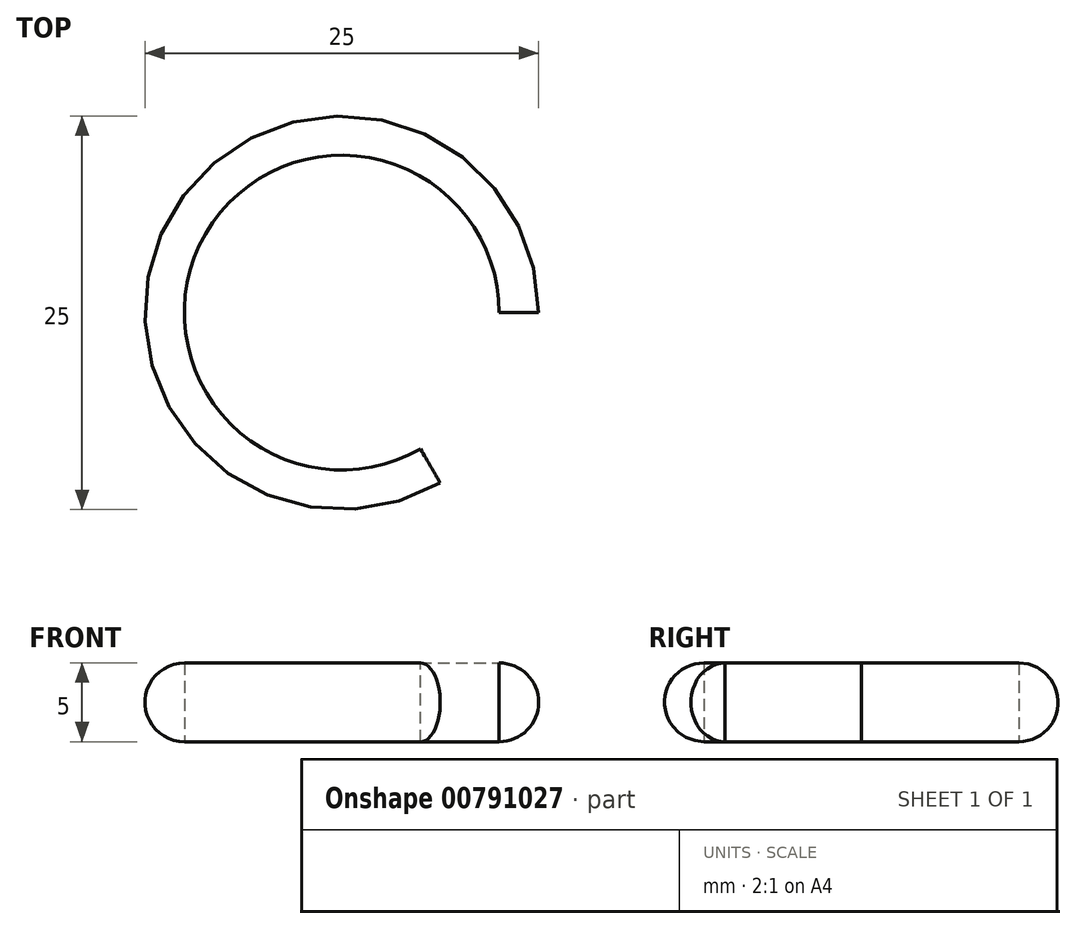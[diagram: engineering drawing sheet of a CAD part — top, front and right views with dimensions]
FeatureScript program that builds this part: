
annotation { "Feature Type Name" : "Feature", "Feature Type Description" : "" }
export const myFeature = defineFeature(function(context is Context, id is Id, definition is map)
    precondition{}
    {
        {
            var Q0;
            Q0=qCreatedBy(makeId("Front.planeOp"),FACE);
            var sketch = newSketch(context, id + "F0", { "sketchPlane" : qUnion([Q0])});
            skLineSegment(sketch, "E0", {"start": v(0, 0) * mm, "end": v(0, 5) * mm});
            skArc(sketch, "E1", {"start": v(0, 0) * mm, "mid": v(2.5, 2.5) * mm, "end": v(0, 5) * mm});
            skLineSegment(sketch, "E2", {"start": v(0, 0) * mm, "end": v(-10, 0) * mm});
            skLineSegment(sketch, "E3", {"start": v(-10, 0) * mm, "end": v(-10, 18.42) * mm});
            skSolve(sketch);
        }
        {
            var Q0;
            Q0 = qSketchRegion(id + "F0", true);
            var Q1;
            Q1=sQuery(id+"F0.wireOp",EDGE,"E3");
            revolve(context, id + "F1", {"surfaceOperationType" : NewSurfaceOperationType.NEW, "entities" : qUnion([Q0]), "axis" : qUnion([Q1]), "revolveType" : RevolveType.ONE_DIRECTION, "angle" : 300 * degree});
        }
    });
